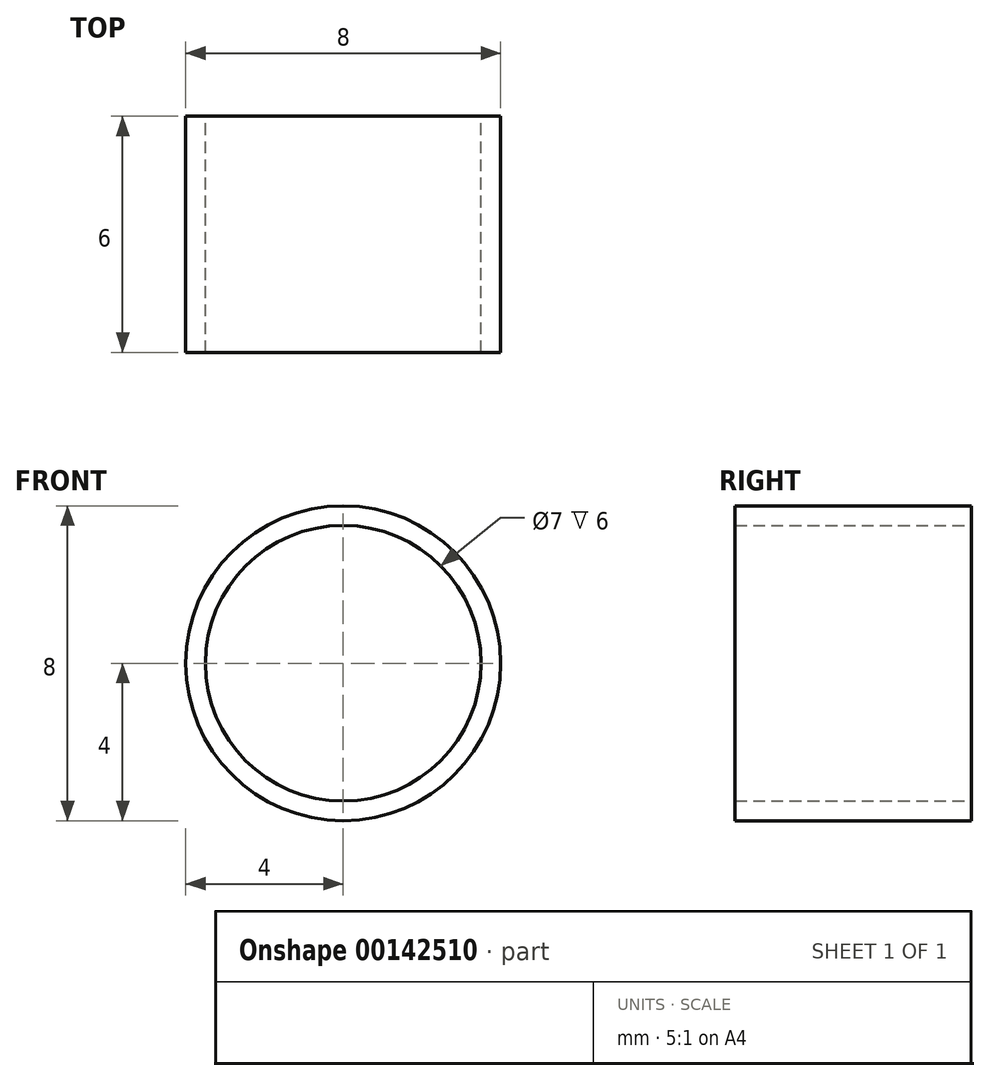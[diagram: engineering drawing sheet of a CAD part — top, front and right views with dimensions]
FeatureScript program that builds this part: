
annotation { "Feature Type Name" : "Feature", "Feature Type Description" : "" }
export const myFeature = defineFeature(function(context is Context, id is Id, definition is map)
    precondition{}
    {
        {
            var Q0;
            Q0=qCreatedBy(makeId("Front.planeOp"),FACE);
            var sketch = newSketch(context, id + "F0", { "sketchPlane" : qUnion([Q0])});
            skCircle(sketch, "E0", {"center": v(0, 0) * mm, "radius": 4 * mm});
            skCircle(sketch, "E1", {"center": v(0, 0) * mm, "radius": 3.5 * mm});
            skSolve(sketch);
        }
        {
            var Q0;
            Q0=makeQuery(id+"F0.imprint","IMPRINT",FACE,{"disambiguationData":[TD([[makeQuery(id+"F0.imprint","IMPRINT",EDGE,{"derivedFrom":sQuery(id+"F0.wireOp",EDGE,"E0")}),1.0]])]});
            extrude(context, id + "F1", {"entities" : qUnion([Q0]), "depth" : 6 * mm});
        }
    });
